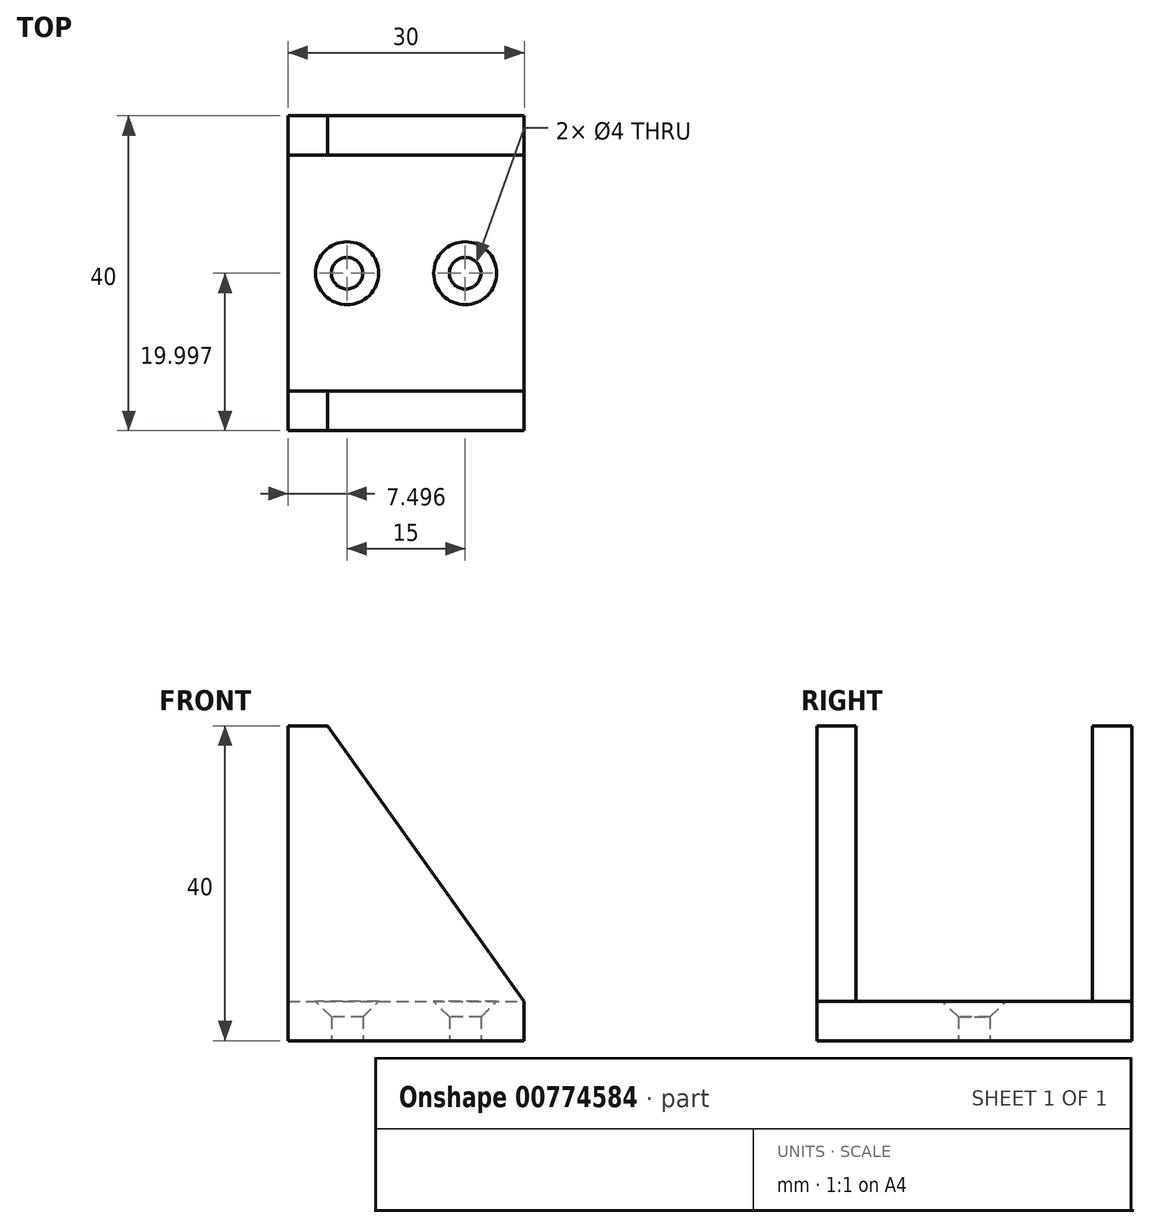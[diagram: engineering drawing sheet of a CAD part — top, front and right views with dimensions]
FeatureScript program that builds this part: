
annotation { "Feature Type Name" : "Feature", "Feature Type Description" : "" }
export const myFeature = defineFeature(function(context is Context, id is Id, definition is map)
    precondition{}
    {
        {
            var Q0;
            Q0=qCreatedBy(makeId("Top.planeOp"),FACE);
            var sketch = newSketch(context, id + "F0", { "sketchPlane" : qUnion([Q0])});
            skLineSegment(sketch, "E0", {"start": v(-103.68, 15.69) * mm, "end": v(-55, 15.69) * mm, "construction": true});
            skLineSegment(sketch, "E1", {"start": v(-82.5, 43.15) * mm, "end": v(-82.5, -1.7) * mm, "construction": true});
            skLineSegment(sketch, "E2", {"start": v(-97.5, 35.69) * mm, "end": v(-67.5, 35.69) * mm});
            skLineSegment(sketch, "E3", {"start": v(-67.5, 35.69) * mm, "end": v(-67.5, -4.31) * mm});
            skLineSegment(sketch, "E4", {"start": v(-67.5, -4.31) * mm, "end": v(-97.5, -4.31) * mm});
            skLineSegment(sketch, "E5", {"start": v(-97.5, -4.31) * mm, "end": v(-97.5, 0.69) * mm});
            skLineSegment(sketch, "E6", {"start": v(-97.5, 0.69) * mm, "end": v(-97.5, 0.69) * mm});
            skLineSegment(sketch, "E7", {"start": v(-97.5, 0.69) * mm, "end": v(-97.5, 30.69) * mm});
            skLineSegment(sketch, "E8", {"start": v(-97.5, 30.69) * mm, "end": v(-97.5, 30.69) * mm});
            skLineSegment(sketch, "E9", {"start": v(-97.5, 30.69) * mm, "end": v(-97.5, 35.69) * mm});
            skCircle(sketch, "E10", {"center": v(-75, 15.69) * mm, "radius": 2 * mm});
            skCircle(sketch, "E11.MirrorC", {"center": v(-90, 15.69) * mm, "radius": 2 * mm});
            skSolve(sketch);
        }
        {
            var Q0;
            Q0=makeQuery(id+"F0.imprint","IMPRINT",FACE,{"disambiguationData":[TD([[makeQuery(id+"F0.imprint","IMPRINT",EDGE,{"derivedFrom":sQuery(id+"F0.wireOp",EDGE,"E2")}),-1.0]])]});
            extrude(context, id + "F1", {"entities" : qUnion([Q0]), "depth" : 5 * mm, "offsetDistance" : 25 * mm});
        }
        {
            var Q0;
            Q0=makeQuery(id+"F1.opExtrude","SWEPT_FACE",FACE,{"disambiguationData":[OSD([sQuery(id+"F0.wireOp",EDGE,"E4")])]});
            var sketch = newSketch(context, id + "F2", { "sketchPlane" : qUnion([Q0])});
            skLineSegment(sketch, "E12", {"start": v(-67.5, 5) * mm, "end": v(-97.5, 5) * mm});
            skLineSegment(sketch, "E13", {"start": v(-97.5, 5) * mm, "end": v(-97.5, 40) * mm});
            skLineSegment(sketch, "E14", {"start": v(-97.5, 40) * mm, "end": v(-92.5, 40) * mm});
            skLineSegment(sketch, "E15", {"start": v(-92.5, 40) * mm, "end": v(-67.5, 5) * mm});
            skSolve(sketch);
        }
        {
            var Q0;
            Q0=makeQuery(id+"F2.imprint","IMPRINT",FACE,{"disambiguationData":[TD([[makeQuery(id+"F2.imprint","IMPRINT",EDGE,{"derivedFrom":sQuery(id+"F2.wireOp",EDGE,"E12")}),-1.0]])]});
            extrude(context, id + "F3", {"entities" : qUnion([Q0]), "operationType" : NewBodyOperationType.ADD, "oppositeDirection" : true, "depth" : 5 * mm, "offsetDistance" : 25 * mm});
        }
        {
            var Q0;
            Q0=makeQuery(id+"F1.opExtrude","SWEPT_FACE",FACE,{"disambiguationData":[OSD([sQuery(id+"F0.wireOp",EDGE,"E2")])]});
            var sketch = newSketch(context, id + "F4", { "sketchPlane" : qUnion([Q0])});
            skLineSegment(sketch, "E16", {"start": v(67.5, 5) * mm, "end": v(97.5, 5) * mm});
            skLineSegment(sketch, "E17", {"start": v(97.5, 5) * mm, "end": v(97.5, 40) * mm});
            skLineSegment(sketch, "E18", {"start": v(97.5, 40) * mm, "end": v(92.5, 40) * mm});
            skLineSegment(sketch, "E19", {"start": v(92.5, 40) * mm, "end": v(67.5, 5) * mm});
            skSolve(sketch);
        }
        {
            var Q0;
            Q0=makeQuery(id+"F4.imprint","IMPRINT",FACE,{"disambiguationData":[TD([[makeQuery(id+"F4.imprint","IMPRINT",EDGE,{"derivedFrom":sQuery(id+"F4.wireOp",EDGE,"E16")}),-1.0]])]});
            extrude(context, id + "F5", {"entities" : qUnion([Q0]), "operationType" : NewBodyOperationType.ADD, "oppositeDirection" : true, "depth" : 5 * mm, "offsetDistance" : 25 * mm});
        }
        {
            var Q0;
            Q0=makeQuery(id+"F1.opExtrude","CAP_EDGE",EDGE,{"disambiguationData":[OSD([sQuery(id+"F0.wireOp",EDGE,"4b1cc655-8edd-429a-9219-c17a1f606dc70.MirrorC")])],"isStart":false});
            var Q1;
            Q1=makeQuery(id+"F1.opExtrude","CAP_EDGE",EDGE,{"disambiguationData":[OSD([sQuery(id+"F0.wireOp",EDGE,"E10")])],"isStart":false});
            var Q2;
            Q2=makeQuery(id+"F1.opExtrude","CAP_EDGE",EDGE,{"disambiguationData":[OSD([sQuery(id+"F0.wireOp",EDGE,"E11.MirrorC")])],"isStart":false});
            chamfer(context, id + "F6", {"entities" : qUnion([Q0, Q1, Q2]), "width" : 2 * mm, "tangentPropagation" : true});
        }
    });
